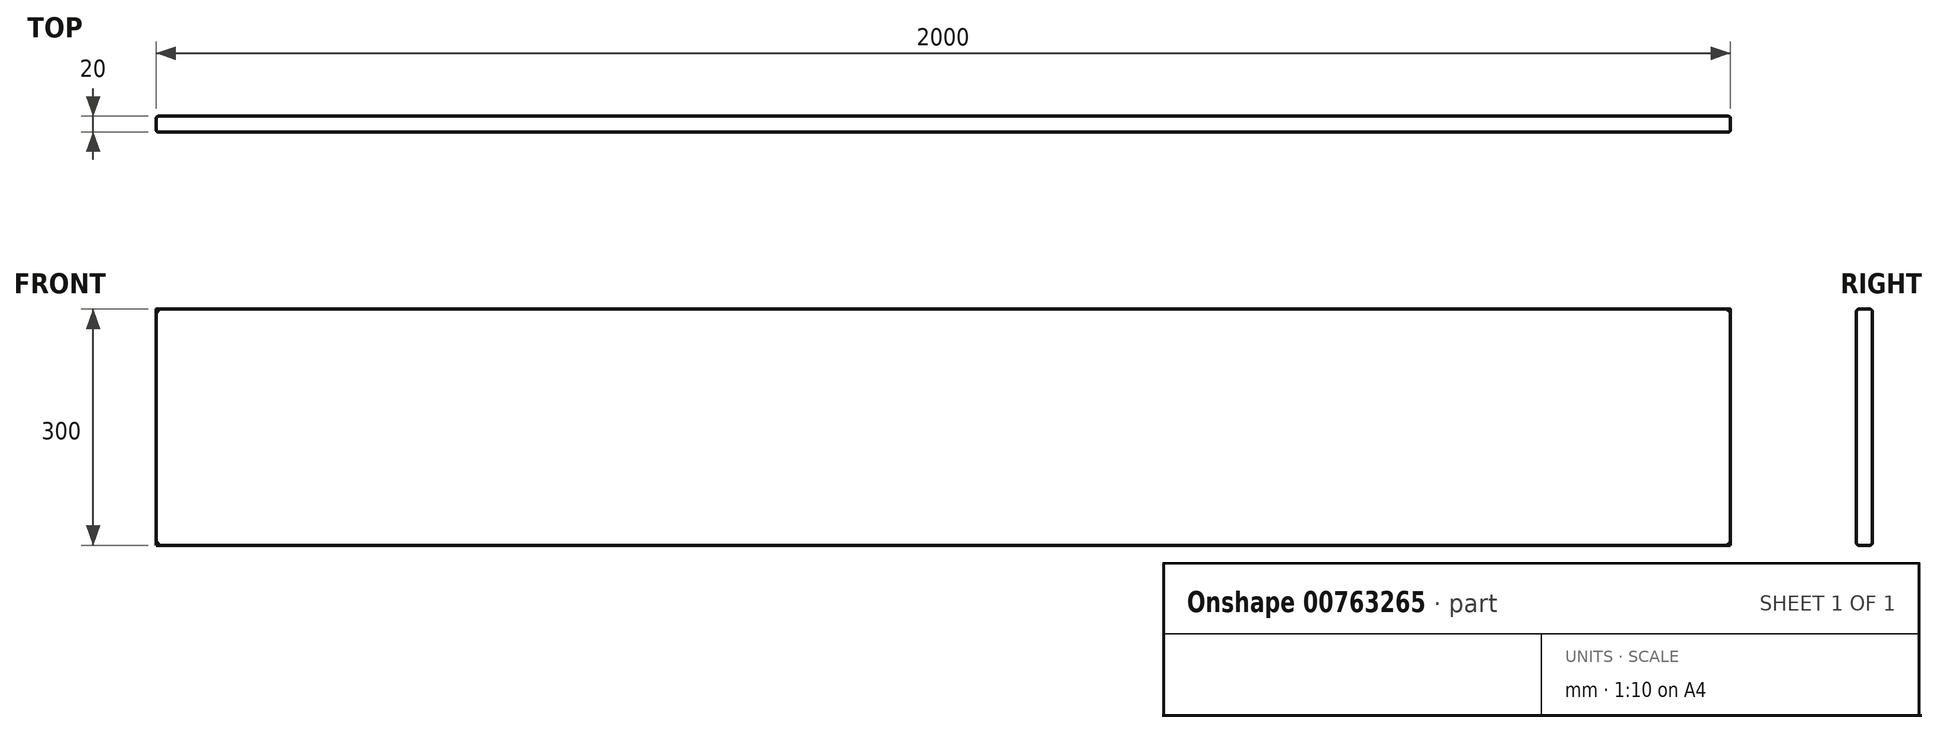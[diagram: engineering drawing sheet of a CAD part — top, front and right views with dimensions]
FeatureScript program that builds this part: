
annotation { "Feature Type Name" : "Feature", "Feature Type Description" : "" }
export const myFeature = defineFeature(function(context is Context, id is Id, definition is map)
    precondition{}
    {
        {
            var Q0;
            Q0=qCreatedBy(makeId("Front.planeOp"),FACE);
            var sketch = newSketch(context, id + "F0", { "sketchPlane" : qUnion([Q0])});
            skLineSegment(sketch, "E0.bottom", {"start": v(0, 0) * mm, "end": v(2000, 0) * mm});
            skLineSegment(sketch, "E0.top", {"start": v(0, 300) * mm, "end": v(2000, 300) * mm});
            skLineSegment(sketch, "E0.left", {"start": v(0, 0) * mm, "end": v(0, 300) * mm});
            skLineSegment(sketch, "E0.right", {"start": v(2000, 0) * mm, "end": v(2000, 300) * mm});
            skSolve(sketch);
        }
        {
            var Q0;
            Q0=makeQuery(id+"F0.imprint","IMPRINT",FACE,{"disambiguationData":[TD([[makeQuery(id+"F0.imprint","IMPRINT",EDGE,{"derivedFrom":sQuery(id+"F0.wireOp",EDGE,"E0.bottom")}),1.0]])]});
            extrude(context, id + "F1", {"entities" : qUnion([Q0]), "depth" : 20 * mm, "offsetDistance" : 25 * mm});
        }
        {
            var Q0;
            Q0=makeQuery(id+"F1.opExtrude","CAP_FACE",FACE,{"disambiguationData":[OSD([sQuery(id+"F0.wireOp",EDGE,"E0.bottom"),sQuery(id+"F0.wireOp",EDGE,"E0.top"),sQuery(id+"F0.wireOp",EDGE,"E0.left"),sQuery(id+"F0.wireOp",EDGE,"E0.right")])],"isStart":false});
            var Q1;
            Q1=makeQuery(id+"F1.opExtrude","CAP_FACE",FACE,{"disambiguationData":[OSD([sQuery(id+"F0.wireOp",EDGE,"E0.bottom"),sQuery(id+"F0.wireOp",EDGE,"E0.top"),sQuery(id+"F0.wireOp",EDGE,"E0.left"),sQuery(id+"F0.wireOp",EDGE,"E0.right")])],"isStart":true});
            fillet(context, id + "F2", {"entities" : qUnion([Q0, Q1]), "radius" : 3 * mm, "tangentPropagation" : true, "allowEdgeOverflow" : false});
        }
        {
            var Q0;
            Q0=makeQuery(id+"F1.opExtrude","CAP_FACE",FACE,{"disambiguationData":[OSD([sQuery(id+"F0.wireOp",EDGE,"E0.bottom"),sQuery(id+"F0.wireOp",EDGE,"E0.top"),sQuery(id+"F0.wireOp",EDGE,"E0.left"),sQuery(id+"F0.wireOp",EDGE,"E0.right")])],"isStart":true});
            var sketch = newSketch(context, id + "F3", { "sketchPlane" : qUnion([Q0])});
            skLineSegment(sketch, "E1", {"start": v(-1000, 3) * mm, "end": v(-1000, 93) * mm});
            skLineSegment(sketch, "E2", {"start": v(-1000, 93) * mm, "end": v(-500, 93) * mm});
            skLineSegment(sketch, "E3", {"start": v(-1000, 93) * mm, "end": v(-1500, 93) * mm});
            skSolve(sketch);
        }
    });
